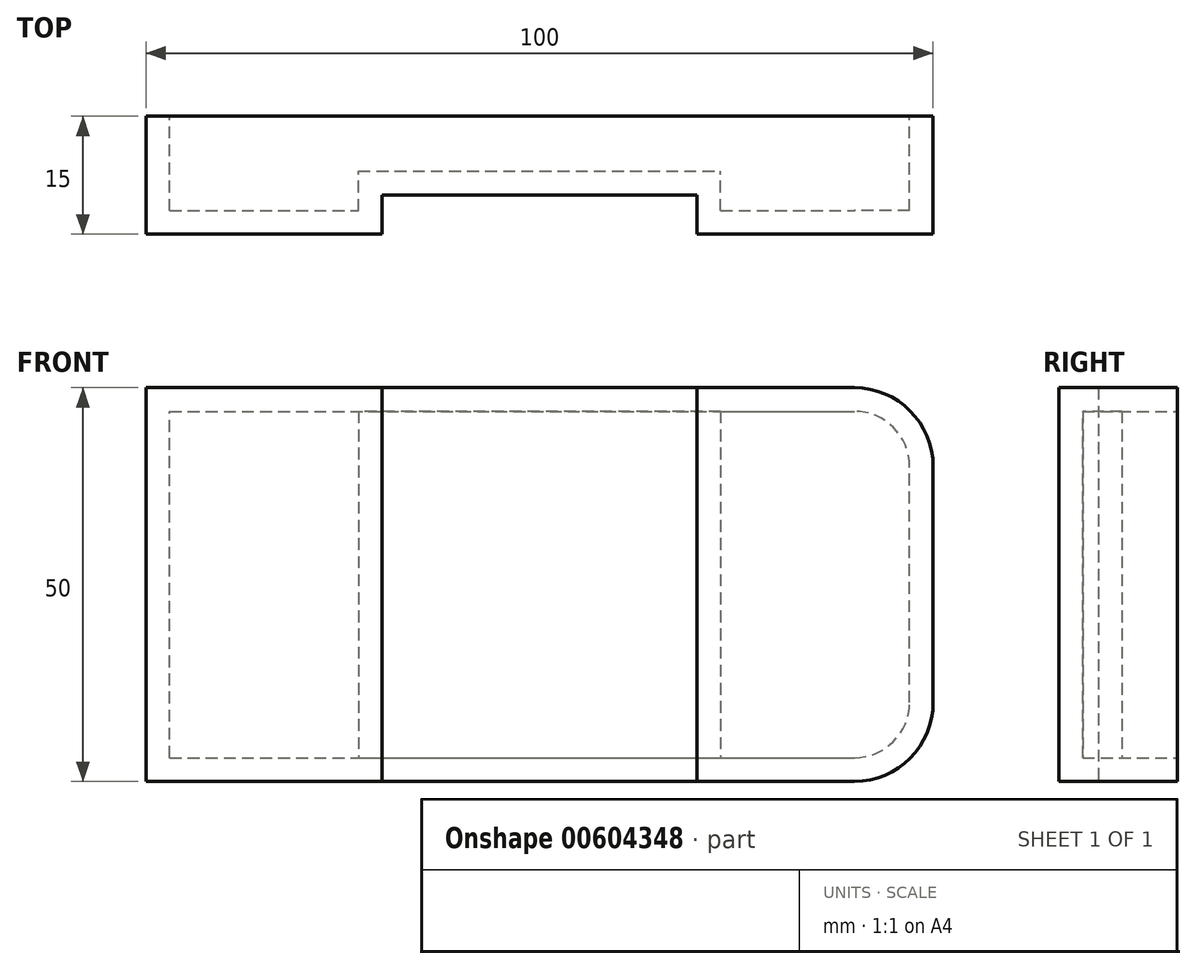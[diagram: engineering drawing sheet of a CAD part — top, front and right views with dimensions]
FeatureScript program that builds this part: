
annotation { "Feature Type Name" : "Feature", "Feature Type Description" : "" }
export const myFeature = defineFeature(function(context is Context, id is Id, definition is map)
    precondition{}
    {
        {
            assignVariable(context, id + "F0", {"name" : "C", "anyValue" : 3});
        }
        {
            var Q0;
            Q0=qCreatedBy(makeId("Front.planeOp"),FACE);
            var sketch = newSketch(context, id + "F1", { "sketchPlane" : qUnion([Q0])});
            skLineSegment(sketch, "E0.bottom", {"start": v(0, 0) * mm, "end": v(100, 0) * mm});
            skLineSegment(sketch, "E0.top", {"start": v(0, 50) * mm, "end": v(100, 50) * mm});
            skLineSegment(sketch, "E0.left", {"start": v(0, 0) * mm, "end": v(0, 50) * mm});
            skLineSegment(sketch, "E0.right", {"start": v(100, 0) * mm, "end": v(100, 50) * mm});
            skSolve(sketch);
        }
        {
            var Q0;
            Q0=makeQuery(id+"F1.imprint","IMPRINT",FACE,{"disambiguationData":[TD([[makeQuery(id+"F1.imprint","IMPRINT",EDGE,{"derivedFrom":sQuery(id+"F1.wireOp",EDGE,"E0.bottom")}),1.0]])]});
            extrude(context, id + "F2", {"entities" : qUnion([Q0]), "depth" : 15 * mm, "offsetDistance" : 25 * mm});
        }
        {
            var Q0;
            Q0=makeQuery(id+"F2.opExtrude","SWEPT_EDGE",EDGE,{"disambiguationData":[OSD([sQuery(id+"F1.wireOp",EDGE,"E0.top"),sQuery(id+"F1.wireOp",EDGE,"E0.right")])]});
            fillet(context, id + "F3", {"entities" : qUnion([Q0]), "radius" : 10 * mm, "tangentPropagation" : true, "allowEdgeOverflow" : false});
        }
        {
            var Q0;
            Q0=makeQuery(id+"F2.opExtrude","SWEPT_EDGE",EDGE,{"disambiguationData":[OSD([sQuery(id+"F1.wireOp",EDGE,"E0.bottom"),sQuery(id+"F1.wireOp",EDGE,"E0.right")])]});
            fillet(context, id + "F4", {"entities" : qUnion([Q0]), "radius" : 10 * mm, "tangentPropagation" : true, "allowEdgeOverflow" : false});
        }
        {
            var Q0;
            Q0=makeQuery(id+"F2.opExtrude","SWEPT_FACE",FACE,{"disambiguationData":[OSD([sQuery(id+"F1.wireOp",EDGE,"E0.bottom")])]});
            var sketch = newSketch(context, id + "F5", { "sketchPlane" : qUnion([Q0])});
            skLineSegment(sketch, "E1.bottom", {"start": v(30, 15) * mm, "end": v(70, 15) * mm});
            skLineSegment(sketch, "E1.top", {"start": v(30, 10) * mm, "end": v(70, 10) * mm});
            skLineSegment(sketch, "E1.left", {"start": v(30, 15) * mm, "end": v(30, 10) * mm});
            skLineSegment(sketch, "E1.right", {"start": v(70, 15) * mm, "end": v(70, 10) * mm});
            skSolve(sketch);
        }
        {
            var Q0;
            Q0=makeQuery(id+"F5.imprint","IMPRINT",FACE,{"disambiguationData":[TD([[makeQuery(id+"F5.imprint","IMPRINT",EDGE,{"derivedFrom":sQuery(id+"F5.wireOp",EDGE,"E1.bottom")}),-1.0]])]});
            extrude(context, id + "F6", {"entities" : qUnion([Q0]), "operationType" : NewBodyOperationType.REMOVE, "endBound" : BoundingType.THROUGH_ALL, "oppositeDirection" : true, "depth" : 25 * mm, "offsetDistance" : 25 * mm});
        }
        {
            var Q0;
            Q0=makeQuery(id+"F2.opExtrude","CAP_FACE",FACE,{"disambiguationData":[OSD([sQuery(id+"F1.wireOp",EDGE,"E0.bottom"),sQuery(id+"F1.wireOp",EDGE,"E0.top"),sQuery(id+"F1.wireOp",EDGE,"E0.left"),sQuery(id+"F1.wireOp",EDGE,"E0.right")])],"isStart":true});
            shell(context, id + "F7", {"entities" : qUnion([Q0]), "thickness" : (getVariable(context, 'C')) * mm});
        }
    });
